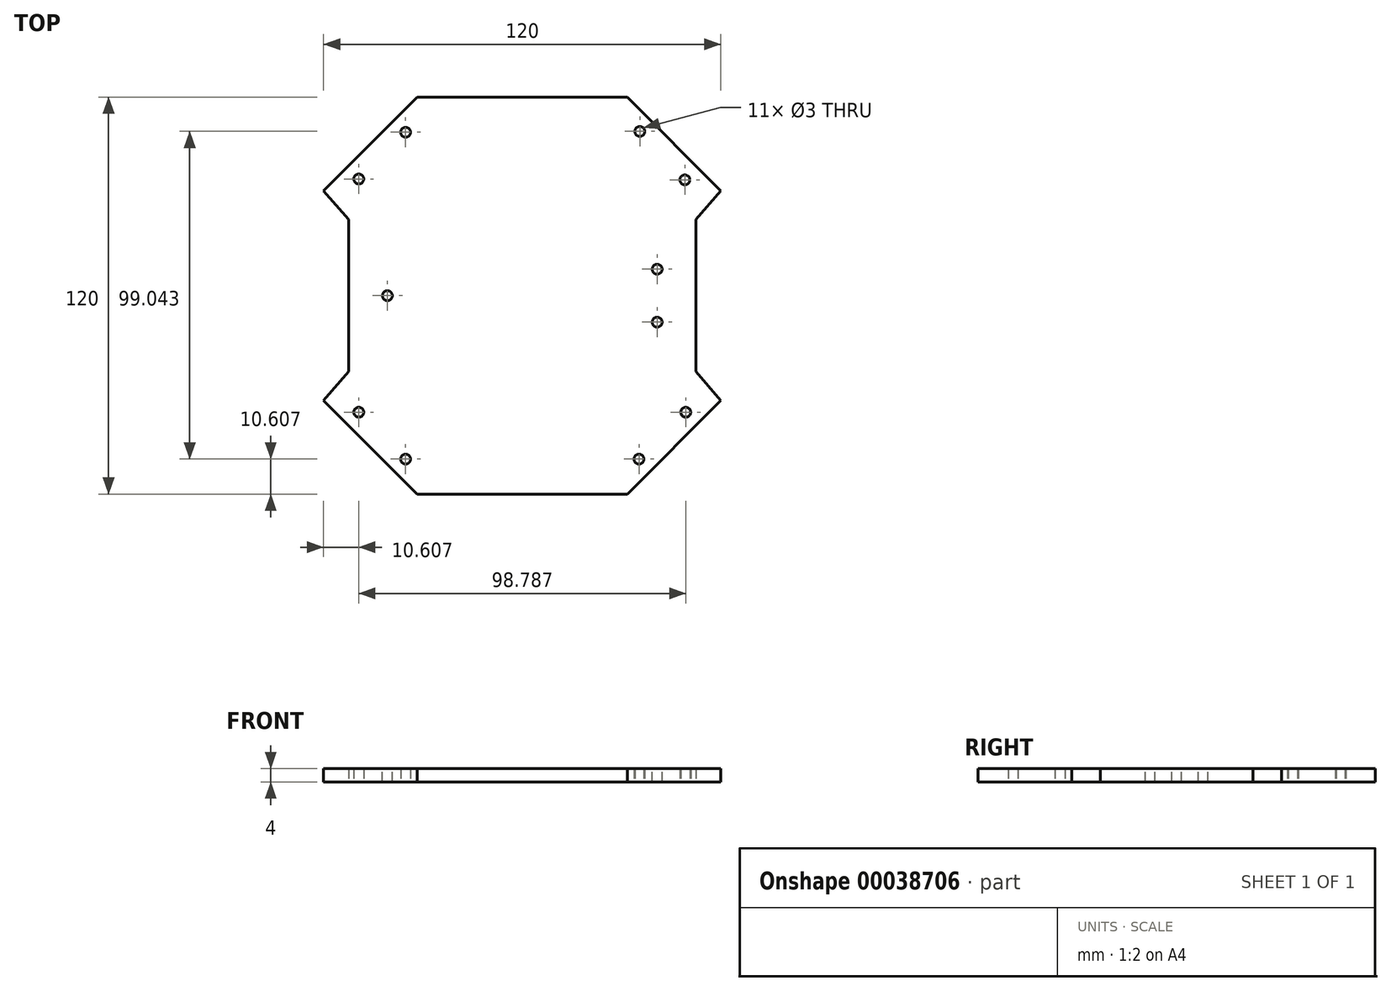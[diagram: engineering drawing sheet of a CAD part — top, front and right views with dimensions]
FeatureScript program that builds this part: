
annotation { "Feature Type Name" : "Feature", "Feature Type Description" : "" }
export const myFeature = defineFeature(function(context is Context, id is Id, definition is map)
    precondition{}
    {
        {
            var Q0;
            Q0=qCreatedBy(makeId("Top.planeOp"),FACE);
            var sketch = newSketch(context, id + "F0", { "sketchPlane" : qUnion([Q0])});
            skLineSegment(sketch, "E0.rect.bottom", {"start": v(32.5, 32.5) * mm, "end": v(-32.5, 32.5) * mm, "construction": true});
            skLineSegment(sketch, "E0.rect.top", {"start": v(32.5, -32.5) * mm, "end": v(-32.5, -32.5) * mm, "construction": true});
            skLineSegment(sketch, "E0.rect.left", {"start": v(32.5, 32.5) * mm, "end": v(32.5, -32.5) * mm, "construction": true});
            skLineSegment(sketch, "E0.rect.right", {"start": v(-32.5, 32.5) * mm, "end": v(-32.5, -32.5) * mm, "construction": true});
            skPoint(sketch, "E0.rect.middle", {"position": v(0, 0) * mm});
            skLineSegment(sketch, "E1", {"start": v(-32.5, -32.5) * mm, "end": v(32.5, 32.5) * mm, "construction": true});
            skLineSegment(sketch, "E2", {"start": v(-32.5, 32.5) * mm, "end": v(32.5, -32.5) * mm, "construction": true});
            skLineSegment(sketch, "E3.bottom", {"start": v(-137.78, 137.78) * mm, "end": v(137.78, 137.78) * mm, "construction": true});
            skLineSegment(sketch, "E3.top", {"start": v(-137.78, -137.78) * mm, "end": v(137.78, -137.78) * mm, "construction": true});
            skLineSegment(sketch, "E3.left", {"start": v(-137.78, 137.78) * mm, "end": v(-137.78, -137.78) * mm, "construction": true});
            skLineSegment(sketch, "E3.right", {"start": v(137.78, 137.78) * mm, "end": v(137.78, -137.78) * mm, "construction": true});
            skCircle(sketch, "E4", {"center": v(-137.78, 137.78) * mm, "radius": 101.5 * mm, "construction": true});
            skCircle(sketch, "E5", {"center": v(137.78, 137.78) * mm, "radius": 101.5 * mm, "construction": true});
            skCircle(sketch, "E6", {"center": v(137.78, -137.78) * mm, "radius": 101.5 * mm, "construction": true});
            skCircle(sketch, "E7", {"center": v(-137.78, -137.78) * mm, "radius": 101.5 * mm, "construction": true});
            skLineSegment(sketch, "E8.rect.bottom", {"start": v(-20.12, 56) * mm, "end": v(20.13, 56) * mm, "construction": true});
            skLineSegment(sketch, "E8.rect.top", {"start": v(-20.13, -56) * mm, "end": v(20.12, -56) * mm, "construction": true});
            skLineSegment(sketch, "E8.rect.left", {"start": v(-20.12, 56) * mm, "end": v(-20.13, -56) * mm, "construction": true});
            skLineSegment(sketch, "E8.rect.right", {"start": v(20.13, 56) * mm, "end": v(20.12, -56) * mm, "construction": true});
            skLineSegment(sketch, "E9.rect.bottom", {"start": v(-45.86, 45.86) * mm, "end": v(45.86, 45.86) * mm, "construction": true});
            skLineSegment(sketch, "E9.rect.top", {"start": v(-45.86, -45.86) * mm, "end": v(45.86, -45.86) * mm, "construction": true});
            skLineSegment(sketch, "E9.rect.left", {"start": v(-45.86, 45.86) * mm, "end": v(-45.86, -45.86) * mm, "construction": true});
            skLineSegment(sketch, "E9.rect.right", {"start": v(45.86, 45.86) * mm, "end": v(45.86, -45.86) * mm, "construction": true});
            skLineSegment(sketch, "E10", {"start": v(45.86, 45.86) * mm, "end": v(137.78, 137.78) * mm, "construction": true});
            skLineSegment(sketch, "E11", {"start": v(45.86, -45.86) * mm, "end": v(137.78, -137.78) * mm, "construction": true});
            skLineSegment(sketch, "E12", {"start": v(0, -137.78) * mm, "end": v(0, 137.78) * mm, "construction": true});
            skLineSegment(sketch, "E13", {"start": v(-137.78, -137.78) * mm, "end": v(-45.86, -45.86) * mm, "construction": true});
            skCircle(sketch, "E14", {"center": v(-137.78, 137.78) * mm, "radius": 14 * mm, "construction": true});
            skCircle(sketch, "E15", {"center": v(-137.78, 137.78) * mm, "radius": 20 * mm});
            skLineSegment(sketch, "E16", {"start": v(-60, 31.72) * mm, "end": v(-60, -31.72) * mm, "construction": true});
            skLineSegment(sketch, "E17", {"start": v(-60, -31.72) * mm, "end": v(-31.72, -60) * mm, "construction": true});
            skLineSegment(sketch, "E18", {"start": v(31.72, -60) * mm, "end": v(60, -31.72) * mm, "construction": true});
            skLineSegment(sketch, "E19", {"start": v(-31.72, -60) * mm, "end": v(31.72, -60) * mm, "construction": true});
            skLineSegment(sketch, "E20", {"start": v(60, -31.72) * mm, "end": v(60, 31.72) * mm, "construction": true});
            skLineSegment(sketch, "E21", {"start": v(31.72, 60) * mm, "end": v(60, 31.72) * mm, "construction": true});
            skLineSegment(sketch, "E22", {"start": v(-31.72, 60) * mm, "end": v(31.72, 60) * mm, "construction": true});
            skLineSegment(sketch, "E23", {"start": v(-151.92, 123.64) * mm, "end": v(-123.64, 151.92) * mm, "construction": true});
            skLineSegment(sketch, "E24", {"start": v(-52.5, 23) * mm, "end": v(-52.5, -23) * mm, "construction": true});
            skLineSegment(sketch, "E25", {"start": v(-52.5, 0) * mm, "end": v(-60, 0) * mm, "construction": true});
            skLineSegment(sketch, "E26", {"start": v(-60, 31.72) * mm, "end": v(-52.5, 23) * mm, "construction": true});
            skLineSegment(sketch, "E27", {"start": v(-60, -31.72) * mm, "end": v(-52.5, -23) * mm, "construction": true});
            skLineSegment(sketch, "E28", {"start": v(52.5, 23) * mm, "end": v(52.5, -23) * mm, "construction": true});
            skLineSegment(sketch, "E29", {"start": v(52.5, 0) * mm, "end": v(60, 0) * mm, "construction": true});
            skLineSegment(sketch, "E30", {"start": v(60, 31.72) * mm, "end": v(52.5, 23) * mm, "construction": true});
            skLineSegment(sketch, "E31", {"start": v(60, -31.72) * mm, "end": v(52.5, -23) * mm, "construction": true});
            skCircle(sketch, "E32", {"center": v(-137.78, -137.78) * mm, "radius": 20 * mm, "construction": true});
            skCircle(sketch, "E33", {"center": v(137.78, -137.78) * mm, "radius": 20 * mm, "construction": true});
            skCircle(sketch, "E34", {"center": v(137.78, 137.78) * mm, "radius": 20 * mm, "construction": true});
            skLineSegment(sketch, "E35", {"start": v(-151.92, -123.64) * mm, "end": v(-123.64, -151.92) * mm, "construction": true});
            skLineSegment(sketch, "E36", {"start": v(123.64, -151.92) * mm, "end": v(151.92, -123.64) * mm, "construction": true});
            skLineSegment(sketch, "E37", {"start": v(151, 122.77) * mm, "end": v(124.57, 152.8) * mm, "construction": true});
            skLineSegment(sketch, "E38", {"start": v(-60, 31.72) * mm, "end": v(-31.72, 60) * mm});
            skLineSegment(sketch, "E39", {"start": v(-45.86, 45.86) * mm, "end": v(-137.78, 137.78) * mm, "construction": true});
            skLineSegment(sketch, "E40", {"start": v(-112.33, 92.53) * mm, "end": v(-92.53, 112.33) * mm, "construction": true});
            skPoint(sketch, "E41", {"position": v(-102.43, 102.43) * mm});
            skLineSegment(sketch, "E42", {"start": v(-151.92, 123.64) * mm, "end": v(-112.33, 92.53) * mm});
            skLineSegment(sketch, "E43", {"start": v(-112.33, 92.53) * mm, "end": v(-60, 31.72) * mm});
            skLineSegment(sketch, "E44", {"start": v(-123.64, 151.92) * mm, "end": v(-92.53, 112.33) * mm});
            skLineSegment(sketch, "E45", {"start": v(-31.72, 60) * mm, "end": v(-92.53, 112.33) * mm});
            skLineSegment(sketch, "E46", {"start": v(-92.53, -112.33) * mm, "end": v(-112.33, -92.53) * mm, "construction": true});
            skPoint(sketch, "E47", {"position": v(-102.43, -102.43) * mm});
            skLineSegment(sketch, "E48", {"start": v(112.33, 92.53) * mm, "end": v(92.53, 112.33) * mm, "construction": true});
            skLineSegment(sketch, "E49", {"start": v(112.33, -92.53) * mm, "end": v(92.53, -112.33) * mm, "construction": true});
            skPoint(sketch, "E50", {"position": v(102.43, 102.43) * mm});
            skPoint(sketch, "E51", {"position": v(102.43, -102.43) * mm});
            skLineSegment(sketch, "E52", {"start": v(124.57, 152.8) * mm, "end": v(92.53, 112.33) * mm, "construction": true});
            skLineSegment(sketch, "E53", {"start": v(31.72, 60) * mm, "end": v(92.53, 112.33) * mm, "construction": true});
            skLineSegment(sketch, "E54", {"start": v(151, 122.77) * mm, "end": v(112.33, 92.53) * mm, "construction": true});
            skLineSegment(sketch, "E55", {"start": v(60, 31.72) * mm, "end": v(112.33, 92.53) * mm, "construction": true});
            skLineSegment(sketch, "E56", {"start": v(151.92, -123.64) * mm, "end": v(112.33, -92.53) * mm, "construction": true});
            skLineSegment(sketch, "E57", {"start": v(112.33, -92.53) * mm, "end": v(60, -31.72) * mm, "construction": true});
            skLineSegment(sketch, "E58", {"start": v(31.72, -60) * mm, "end": v(92.53, -112.33) * mm, "construction": true});
            skLineSegment(sketch, "E59", {"start": v(123.64, -151.92) * mm, "end": v(92.53, -112.33) * mm, "construction": true});
            skLineSegment(sketch, "E60", {"start": v(-123.64, -151.92) * mm, "end": v(-92.53, -112.33) * mm, "construction": true});
            skLineSegment(sketch, "E61", {"start": v(-31.72, -60) * mm, "end": v(-92.53, -112.33) * mm, "construction": true});
            skLineSegment(sketch, "E62", {"start": v(-60, -31.72) * mm, "end": v(-112.33, -92.53) * mm, "construction": true});
            skLineSegment(sketch, "E63", {"start": v(-151.92, -123.64) * mm, "end": v(-112.33, -92.53) * mm, "construction": true});
            skLineSegment(sketch, "E64", {"start": v(-53.46, 24.11) * mm, "end": v(-24.11, 53.46) * mm});
            skLineSegment(sketch, "E65", {"start": v(-24.11, 53.46) * mm, "end": v(-31.72, 60) * mm});
            skLineSegment(sketch, "E66", {"start": v(-53.46, 24.11) * mm, "end": v(-60, 31.72) * mm});
            skSolve(sketch);
        }
        {
            var Q0;
            Q0=qCreatedBy(makeId("Top.planeOp"),FACE);
            var sketch = newSketch(context, id + "F1", { "sketchPlane" : qUnion([Q0])});
            skLineSegment(sketch, "E67.0", {"start": v(-151.92, 123.64) * mm, "end": v(-112.33, 92.53) * mm});
            skLineSegment(sketch, "E68.0", {"start": v(-112.33, 92.53) * mm, "end": v(-60, 31.72) * mm});
            skLineSegment(sketch, "E68.1", {"start": v(-31.72, 60) * mm, "end": v(-92.53, 112.33) * mm});
            skLineSegment(sketch, "E68.2", {"start": v(-123.64, 151.92) * mm, "end": v(-92.53, 112.33) * mm});
            skCircle(sketch, "E68.3", {"center": v(-137.78, 137.78) * mm, "radius": 20 * mm});
            skLineSegment(sketch, "E68.4", {"start": v(-24.11, 53.46) * mm, "end": v(-31.72, 60) * mm});
            skLineSegment(sketch, "E68.5", {"start": v(-53.46, 24.11) * mm, "end": v(-60, 31.72) * mm});
            skLineSegment(sketch, "E68.6", {"start": v(-53.46, 24.11) * mm, "end": v(-24.11, 53.46) * mm});
            skSolve(sketch);
        }
        {
            var Q0;
            Q0=makeQuery(id+"FJeBJDLh8THmY7t_0.opExtrude","CAP_FACE",FACE,{"disambiguationData":[OSD([sQuery(id+"F1.wireOp",EDGE,"E67.0"),sQuery(id+"F1.wireOp",EDGE,"E68.0"),sQuery(id+"F1.wireOp",EDGE,"E68.1"),sQuery(id+"F1.wireOp",EDGE,"E68.2"),sQuery(id+"F1.wireOp",EDGE,"E68.3"),sQuery(id+"F1.wireOp",EDGE,"E68.4"),sQuery(id+"F1.wireOp",EDGE,"E68.5"),sQuery(id+"F1.wireOp",EDGE,"E68.6")])],"isStart":false});
            var sketch = newSketch(context, id + "F2", { "sketchPlane" : qUnion([Q0])});
            skCircle(sketch, "E69.0", {"center": v(-137.78, -137.78) * mm, "radius": 20 * mm});
            skLineSegment(sketch, "E70.0", {"start": v(-60, -31.72) * mm, "end": v(-31.72, -60) * mm});
            skLineSegment(sketch, "E71.0", {"start": v(-24.11, -53.46) * mm, "end": v(-49.65, -27.92) * mm});
            skLineSegment(sketch, "E71.1", {"start": v(-92.53, -112.33) * mm, "end": v(-24.11, -53.46) * mm});
            skLineSegment(sketch, "E71.2", {"start": v(-120.9, -148.43) * mm, "end": v(-92.53, -112.33) * mm});
            skLineSegment(sketch, "E72.0", {"start": v(-109.55, -95.43) * mm, "end": v(-145.9, -124) * mm});
            skLineSegment(sketch, "E72.1", {"start": v(-124, -145.9) * mm, "end": v(-95.43, -109.55) * mm});
            skLineSegment(sketch, "E72.2", {"start": v(-95.43, -109.55) * mm, "end": v(-34.55, -57.16) * mm});
            skArc(sketch, "E72.3", {"start": v(-145.9, -124) * mm, "mid": v(-149.1, -149.1) * mm, "end": v(-124, -145.9) * mm});
            skLineSegment(sketch, "E72.5", {"start": v(-57.16, -34.55) * mm, "end": v(-109.55, -95.43) * mm});
            skLineSegment(sketch, "E73.0", {"start": v(-45.86, -45.86) * mm, "end": v(-123.64, -123.64) * mm, "construction": true});
            skLineSegment(sketch, "E74.0", {"start": v(-46.92, -44.8) * mm, "end": v(-124.74, -122.62) * mm});
            skLineSegment(sketch, "E75.0", {"start": v(-44.8, -46.92) * mm, "end": v(-122.62, -124.74) * mm});
            skSolve(sketch);
        }
        {
            var Q0;
            Q0=makeQuery(id+"FfZ2kWWbx0hkoDQ_1.boolean.opBoolean","MERGE",FACE,{"derivedFrom":[makeQuery(id+"FJeBJDLh8THmY7t_0.opExtrude","CAP_FACE",FACE,{"disambiguationData":[OSD([sQuery(id+"F1.wireOp",EDGE,"E67.0"),sQuery(id+"F1.wireOp",EDGE,"E68.0"),sQuery(id+"F1.wireOp",EDGE,"E68.1"),sQuery(id+"F1.wireOp",EDGE,"E68.2"),sQuery(id+"F1.wireOp",EDGE,"E68.3"),sQuery(id+"F1.wireOp",EDGE,"E68.4"),sQuery(id+"F1.wireOp",EDGE,"E68.5"),sQuery(id+"F1.wireOp",EDGE,"E68.6")])],"isStart":false}),makeQuery(id+"FfZ2kWWbx0hkoDQ_1.opExtrude","CAP_FACE",FACE,{"disambiguationData":[OSD([sQuery(id+"F2.wireOp",EDGE,"E72.0"),sQuery(id+"F2.wireOp",EDGE,"E72.1"),sQuery(id+"F2.wireOp",EDGE,"E72.2"),sQuery(id+"F2.wireOp",EDGE,"E72.5"),sQuery(id+"F2.wireOp",EDGE,"E74.0"),sQuery(id+"F2.wireOp",EDGE,"E75.0"),sQuery(id+"FiQxRTnNKV71TQx_1.wireOp",EDGE,"38970236-bfd6-4454-96b1-5af9a77133ed.0"),sQuery(id+"FiQxRTnNKV71TQx_1.wireOp",EDGE,"38970236-bfd6-4454-96b1-5af9a77133ed.1"),sQuery(id+"FiQxRTnNKV71TQx_1.wireOp",EDGE,"38970236-bfd6-4454-96b1-5af9a77133ed.2"),sQuery(id+"FiQxRTnNKV71TQx_1.wireOp",EDGE,"38970236-bfd6-4454-96b1-5af9a77133ed.3"),sQuery(id+"FiQxRTnNKV71TQx_1.wireOp",EDGE,"38970236-bfd6-4454-96b1-5af9a77133ed.4"),sQuery(id+"FiQxRTnNKV71TQx_1.wireOp",EDGE,"38970236-bfd6-4454-96b1-5af9a77133ed.5"),sQuery(id+"FiQxRTnNKV71TQx_1.wireOp",EDGE,"38970236-bfd6-4454-96b1-5af9a77133ed.6"),sQuery(id+"FiQxRTnNKV71TQx_1.wireOp",EDGE,"38970236-bfd6-4454-96b1-5af9a77133ed.7"),sQuery(id+"FiQxRTnNKV71TQx_1.wireOp",EDGE,"38970236-bfd6-4454-96b1-5af9a77133ed.11"),sQuery(id+"FiQxRTnNKV71TQx_1.wireOp",EDGE,"84821af2-2a79-4291-835d-9572d2859dc5.1"),sQuery(id+"FiQxRTnNKV71TQx_1.wireOp",EDGE,"84821af2-2a79-4291-835d-9572d2859dc5.2"),sQuery(id+"FiQxRTnNKV71TQx_1.wireOp",EDGE,"84821af2-2a79-4291-835d-9572d2859dc5.3"),sQuery(id+"FiQxRTnNKV71TQx_1.wireOp",EDGE,"84821af2-2a79-4291-835d-9572d2859dc5.4"),sQuery(id+"FiQxRTnNKV71TQx_1.wireOp",EDGE,"84821af2-2a79-4291-835d-9572d2859dc5.5"),sQuery(id+"FiQxRTnNKV71TQx_1.wireOp",EDGE,"84821af2-2a79-4291-835d-9572d2859dc5.6"),sQuery(id+"FiQxRTnNKV71TQx_1.wireOp",EDGE,"84821af2-2a79-4291-835d-9572d2859dc5.7"),sQuery(id+"FiQxRTnNKV71TQx_1.wireOp",EDGE,"84821af2-2a79-4291-835d-9572d2859dc5.8"),sQuery(id+"FiQxRTnNKV71TQx_1.wireOp",EDGE,"84821af2-2a79-4291-835d-9572d2859dc5.11"),sQuery(id+"FiQxRTnNKV71TQx_1.wireOp",EDGE,"8611adc8-e619-4c53-af6e-c2d4046b9e3c0.MirrorCS"),sQuery(id+"FiQxRTnNKV71TQx_1.wireOp",EDGE,"d0435597-b384-4ab9-9637-6f22e2db63830.MirrorCS"),sQuery(id+"FiQxRTnNKV71TQx_1.wireOp",EDGE,"db108342-3424-454d-b83c-aa2f3f1c2cb20.MirrorCS"),sQuery(id+"FiQxRTnNKV71TQx_1.wireOp",EDGE,"8967fe85-72d8-4dfa-971c-bef20ae89da20.MirrorCS"),sQuery(id+"FiQxRTnNKV71TQx_1.wireOp",EDGE,"f7285943-b11e-44b1-814a-c0c81710d16c0.MirrorCS"),sQuery(id+"FiQxRTnNKV71TQx_1.wireOp",EDGE,"30e0d23f-14ae-41a2-b20f-fbc5a62c98db0.MirrorCS"),sQuery(id+"FiQxRTnNKV71TQx_1.wireOp",EDGE,"1f170661-e214-4223-ba55-c6e99d467d940.MirrorCS"),sQuery(id+"FiQxRTnNKV71TQx_1.wireOp",EDGE,"0d6bcc0d-2ce1-4a65-832b-dffd11caf7e80.MirrorCS"),sQuery(id+"FiQxRTnNKV71TQx_1.wireOp",EDGE,"7abc0380-5524-41c7-a0ce-68a4796d5a7b0.MirrorCS"),sQuery(id+"FiQxRTnNKV71TQx_1.wireOp",EDGE,"19e96206-981b-43be-ba05-1c10bb68f1450.MirrorCS"),sQuery(id+"FiQxRTnNKV71TQx_1.wireOp",EDGE,"2ea1ab67-ca09-4ed3-820a-d74567cfc47a0.MirrorCS"),sQuery(id+"FiQxRTnNKV71TQx_1.wireOp",EDGE,"91afe6bc-90b4-4b5e-82f6-75096f2b2aa40.MirrorCS"),sQuery(id+"FiQxRTnNKV71TQx_1.wireOp",EDGE,"e83ae27f-a570-4dcf-a388-984b5eeb59020.MirrorCS"),sQuery(id+"FiQxRTnNKV71TQx_1.wireOp",EDGE,"90c546e3-c060-4be6-aa96-ffa96f1bf26c0.MirrorCS"),sQuery(id+"FiQxRTnNKV71TQx_1.wireOp",EDGE,"99bcaea7-dbcd-4b30-a0d6-bc1ef52a4ca00.MirrorCS"),sQuery(id+"FiQxRTnNKV71TQx_1.wireOp",EDGE,"c8000fa1-2a0c-4d24-8a33-407feac34fb10.MirrorCS"),sQuery(id+"FiQxRTnNKV71TQx_1.wireOp",EDGE,"3c656657-db58-4b72-afe2-c262a7839c5d0.MirrorCS"),sQuery(id+"FiQxRTnNKV71TQx_1.wireOp",EDGE,"813f3043-2374-4368-9225-d27bba9bf23f0.MirrorCS"),sQuery(id+"FiQxRTnNKV71TQx_1.wireOp",EDGE,"YwUhEMed-aB1d-ipUQ-UnQH-Itm6UoLuJCMO"),sQuery(id+"FiQxRTnNKV71TQx_1.wireOp",EDGE,"h0J1Apl3-0yBk-VO02-KO2W-2kVpn1Ds907W"),sQuery(id+"FiQxRTnNKV71TQx_1.wireOp",EDGE,"vqShVz5m-KmEU-cyHf-AfiJ-yMXPyKyrkMLc"),sQuery(id+"FiQxRTnNKV71TQx_1.wireOp",EDGE,"wBHHw6Ij-qgAp-Wx4X-vHHM-6AXWrW058tig"),sQuery(id+"FiQxRTnNKV71TQx_1.wireOp",EDGE,"UQsRDA6M-BFFb-5RWh-NpgG-BJ7fZ36mSHP9"),sQuery(id+"FiQxRTnNKV71TQx_1.wireOp",EDGE,"gtlBCoMz-qEui-tsZH-9I7z-61eOqyYzUrIE"),sQuery(id+"FiQxRTnNKV71TQx_1.wireOp",EDGE,"5JgQ3pHy-WNFa-i7Q0-qU2A-RRM7FCAXBTSd"),sQuery(id+"FiQxRTnNKV71TQx_1.wireOp",EDGE,"w7owdK0z-TjIJ-COOg-YfHl-q6q5tVCwM537")])],"isStart":true})]});
            var sketch = newSketch(context, id + "F3", { "sketchPlane" : qUnion([Q0])});
            skLineSegment(sketch, "E76", {"start": v(-151.92, -151.92) * mm, "end": v(-38.79, -38.79) * mm, "construction": true});
            skArc(sketch, "E77.0", {"start": v(-120.7, -148.18) * mm, "mid": v(-151.92, -151.92) * mm, "end": v(-148.18, -120.7) * mm, "construction": true});
            skLineSegment(sketch, "E78", {"start": v(-137.78, -129.78) * mm, "end": v(-137.78, -145.78) * mm, "construction": true});
            skPoint(sketch, "E78.startSnap0", {"position": v(-137.78, -131.9) * mm});
            skLineSegment(sketch, "E79", {"start": v(-147.28, -137.78) * mm, "end": v(-128.28, -137.78) * mm, "construction": true});
            skPoint(sketch, "E80", {"position": v(-137.78, -129.78) * mm});
            skPoint(sketch, "E81", {"position": v(-128.28, -137.78) * mm});
            skPoint(sketch, "E82", {"position": v(-137.78, -145.78) * mm});
            skPoint(sketch, "E83", {"position": v(-147.28, -137.78) * mm});
            skLineSegment(sketch, "E84", {"start": v(-31.72, -60) * mm, "end": v(-24.64, -52.93) * mm, "construction": true});
            skLineSegment(sketch, "E85", {"start": v(-45.86, -45.86) * mm, "end": v(-38.79, -38.79) * mm, "construction": true});
            skPoint(sketch, "E86", {"position": v(-42.32, -42.32) * mm});
            skLineSegment(sketch, "E87", {"start": v(-49.4, -35.25) * mm, "end": v(-35.25, -49.4) * mm, "construction": true});
            skCircle(sketch, "E88", {"center": v(-137.78, -137.78) * mm, "radius": 4 * mm});
            skSolve(sketch);
        }
        {
            var Q0;
            Q0=qCreatedBy(makeId("Top.planeOp"),FACE);
            var sketch = newSketch(context, id + "F4", { "sketchPlane" : qUnion([Q0])});
            skLineSegment(sketch, "E89.0", {"start": v(-31.72, 60) * mm, "end": v(31.72, 60) * mm});
            skLineSegment(sketch, "E89.1", {"start": v(-60, 31.72) * mm, "end": v(-31.72, 60) * mm});
            skLineSegment(sketch, "E89.2", {"start": v(-60, 31.72) * mm, "end": v(-52.5, 23) * mm});
            skLineSegment(sketch, "E89.3", {"start": v(-52.5, 23) * mm, "end": v(-52.5, -23) * mm});
            skLineSegment(sketch, "E89.4", {"start": v(-60, -31.72) * mm, "end": v(-52.5, -23) * mm});
            skLineSegment(sketch, "E89.5", {"start": v(-60, -31.72) * mm, "end": v(-31.72, -60) * mm});
            skLineSegment(sketch, "E89.6", {"start": v(-31.72, -60) * mm, "end": v(31.72, -60) * mm});
            skLineSegment(sketch, "E89.7", {"start": v(31.72, -60) * mm, "end": v(60, -31.72) * mm});
            skLineSegment(sketch, "E89.8", {"start": v(31.72, 60) * mm, "end": v(60, 31.72) * mm});
            skLineSegment(sketch, "E89.9", {"start": v(60, 31.72) * mm, "end": v(52.5, 23) * mm});
            skLineSegment(sketch, "E89.10", {"start": v(60, -31.72) * mm, "end": v(52.5, -23) * mm});
            skLineSegment(sketch, "E89.11", {"start": v(52.5, 23) * mm, "end": v(52.5, -23) * mm});
            skLineSegment(sketch, "E89.12", {"start": v(-49.4, 35.25) * mm, "end": v(-35.25, 49.4) * mm});
            skPoint(sketch, "E89.13", {"position": v(-35.25, 49.4) * mm});
            skPoint(sketch, "E89.14", {"position": v(-49.4, 35.25) * mm});
            skLineSegment(sketch, "E89.15", {"start": v(-53.46, 24.11) * mm, "end": v(-60, 31.72) * mm});
            skLineSegment(sketch, "E90", {"start": v(-42.32, 42.32) * mm, "end": v(-45.86, 45.86) * mm});
            skLineSegment(sketch, "E91", {"start": v(45.86, 45.86) * mm, "end": v(42.32, 42.32) * mm});
            skLineSegment(sketch, "E92", {"start": v(35.52, 49.65) * mm, "end": v(49.13, 35) * mm});
            skLineSegment(sketch, "E93", {"start": v(45.86, -45.86) * mm, "end": v(42.32, -42.32) * mm});
            skLineSegment(sketch, "E94", {"start": v(-45.86, -45.86) * mm, "end": v(-42.32, -42.32) * mm});
            skLineSegment(sketch, "E95", {"start": v(-49.4, -35.25) * mm, "end": v(-35.25, -49.4) * mm});
            skLineSegment(sketch, "E96", {"start": v(35.25, -49.4) * mm, "end": v(49.4, -35.25) * mm});
            skSolve(sketch);
        }
        {
            var Q0;
            {var subQ1=sQuery(id+"F4.wireOp",EDGE,"E89.0");Q0=makeQuery(id+"F4.imprint","IMPRINT",FACE,{"disambiguationData":[TD([[makeQuery(id+"F4.imprint","IMPRINT",EDGE,{"derivedFrom":subQ1}),-1.0]])]});}
            extrude(context, id + "F5", {"entities" : qUnion([Q0]), "depth" : 4 * mm});
        }
        {
            var Q0;
            Q0=makeQuery(id+"F5.opExtrude","CAP_FACE",FACE,{"disambiguationData":[OSD([sQuery(id+"F4.wireOp",EDGE,"E89.0"),sQuery(id+"F4.wireOp",EDGE,"E89.2"),sQuery(id+"F4.wireOp",EDGE,"E89.3"),sQuery(id+"F4.wireOp",EDGE,"E89.4"),sQuery(id+"F4.wireOp",EDGE,"E89.5"),sQuery(id+"F4.wireOp",EDGE,"E89.6"),sQuery(id+"F4.wireOp",EDGE,"E89.7"),sQuery(id+"F4.wireOp",EDGE,"E89.8"),sQuery(id+"F4.wireOp",EDGE,"E89.9"),sQuery(id+"F4.wireOp",EDGE,"E89.10"),sQuery(id+"F4.wireOp",EDGE,"E89.11"),sQuery(id+"F4.wireOp",EDGE,"E89.15"),sQuery(id+"F4.wireOp",EDGE,"E89.1")])],"isStart":false});
            var sketch = newSketch(context, id + "F6", { "sketchPlane" : qUnion([Q0])});
            skLineSegment(sketch, "E97", {"start": v(0, -60) * mm, "end": v(0, 60) * mm, "construction": true});
            skLineSegment(sketch, "E98", {"start": v(-52.5, 0) * mm, "end": v(52.5, 0) * mm, "construction": true});
            skPoint(sketch, "E99", {"position": v(0, 0) * mm});
            skPoint(sketch, "E100", {"position": v(-40.75, 0) * mm});
            skPoint(sketch, "E101", {"position": v(40.75, 0) * mm});
            skLineSegment(sketch, "E102", {"start": v(-40.75, 0) * mm, "end": v(40.75, 0) * mm});
            skLineSegment(sketch, "E103", {"start": v(40.75, 8) * mm, "end": v(40.75, -8) * mm});
            skSolve(sketch);
        }
        {
            var Q0;
            Q0=sQuery(id+"F6.wireOp",VERTEX,"E100");
            var Q1;
            Q1=sQuery(id+"F6.wireOp",VERTEX,"E103.end");
            var Q2;
            Q2=sQuery(id+"F6.wireOp",VERTEX,"E103.start");
            var Q3;
            Q3=makeQuery(id+"F5.opExtrude","SWEPT_BODY",BODY,{"disambiguationData":[OSD([sQuery(id+"F4.wireOp",EDGE,"E89.0"),sQuery(id+"F4.wireOp",EDGE,"E89.2"),sQuery(id+"F4.wireOp",EDGE,"E89.3"),sQuery(id+"F4.wireOp",EDGE,"E89.4"),sQuery(id+"F4.wireOp",EDGE,"E89.5"),sQuery(id+"F4.wireOp",EDGE,"E89.6"),sQuery(id+"F4.wireOp",EDGE,"E89.7"),sQuery(id+"F4.wireOp",EDGE,"E89.8"),sQuery(id+"F4.wireOp",EDGE,"E89.9"),sQuery(id+"F4.wireOp",EDGE,"E89.10"),sQuery(id+"F4.wireOp",EDGE,"E89.11"),sQuery(id+"F4.wireOp",EDGE,"E89.15"),sQuery(id+"F4.wireOp",EDGE,"E89.1")])]});
            hole(context, id + "F7", {"style" : HoleStyle.SIMPLE, "holeDiameter" : 3 * mm, "endStyle" : HoleEndStyle.THROUGH, "locations" : qUnion([Q0, Q1, Q2]), "scope" : qUnion([Q3])});
        }
        {
            var Q0;
            Q0=sQuery(id+"F4.wireOp",VERTEX,"E89.14");
            var Q1;
            Q1=sQuery(id+"F4.wireOp",VERTEX,"E89.13");
            var Q2;
            Q2=sQuery(id+"F4.wireOp",VERTEX,"E92.start");
            var Q3;
            Q3=sQuery(id+"F4.wireOp",VERTEX,"E92.end");
            var Q4;
            Q4=sQuery(id+"F4.wireOp",VERTEX,"E96.end");
            var Q5;
            Q5=sQuery(id+"F4.wireOp",VERTEX,"E96.start");
            var Q6;
            Q6=sQuery(id+"F4.wireOp",VERTEX,"E95.end");
            var Q7;
            Q7=sQuery(id+"F4.wireOp",VERTEX,"E95.start");
            var Q8;
            Q8=makeQuery(id+"F5.opExtrude","SWEPT_BODY",BODY,{"disambiguationData":[OSD([sQuery(id+"F4.wireOp",EDGE,"E89.0"),sQuery(id+"F4.wireOp",EDGE,"E89.2"),sQuery(id+"F4.wireOp",EDGE,"E89.3"),sQuery(id+"F4.wireOp",EDGE,"E89.4"),sQuery(id+"F4.wireOp",EDGE,"E89.5"),sQuery(id+"F4.wireOp",EDGE,"E89.6"),sQuery(id+"F4.wireOp",EDGE,"E89.7"),sQuery(id+"F4.wireOp",EDGE,"E89.8"),sQuery(id+"F4.wireOp",EDGE,"E89.9"),sQuery(id+"F4.wireOp",EDGE,"E89.10"),sQuery(id+"F4.wireOp",EDGE,"E89.11"),sQuery(id+"F4.wireOp",EDGE,"E89.15"),sQuery(id+"F4.wireOp",EDGE,"E89.1")])]});
            hole(context, id + "F8", {"style" : HoleStyle.SIMPLE, "holeDiameter" : 3 * mm, "endStyle" : HoleEndStyle.THROUGH, "oppositeDirection" : true, "locations" : qUnion([Q0, Q1, Q2, Q3, Q4, Q5, Q6, Q7]), "scope" : qUnion([Q8])});
        }
    });
